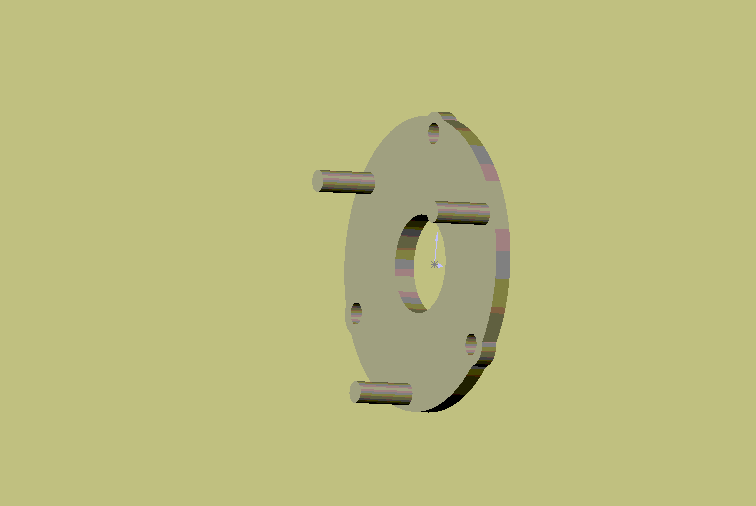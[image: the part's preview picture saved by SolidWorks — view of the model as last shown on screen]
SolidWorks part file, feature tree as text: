
SOLIDWORKS PART (.sldprt)
format: sldprt  version: not decoded by parser v0  size: 128,512 bytes
history: native  units: mm
features: sketch x5, plane x3, extrude x3, cut_extrude x2, material x1 (+8 scaffold rows collapsed)
feature tree (22):
  scaffold x8  (default folders/planes/origin — collapsed)
  material  "Matériau <non spécifié>"
  plane  "Plane1"
  plane  "Plane2"
  plane  "Plane3"
  sketch  "Esquisse1"  dims[D1=27.0mm D2=4.0mm D4=4.0mm D3=12.0mm]
  extrude  "Base-Extrusion"  Depth=1.5mm
  sketch  "Esquisse2"  dims[D1=2.0mm D2=2.0mm]
  cut_extrude  "Enlèv. mat.-Extru.1"  [1 undecoded]
  sketch  "Esquisse3"  dims[c1.D2=2.0mm c1.D1=18.0mm c2.D1=30.0deg c2.D3=12.0mm]
  extrude  "Boss.-Extru.1"  Depth=5.5mm
  sketch  "Esquisse4"  dims[D1=12.0mm]
  extrude  "Boss.-Extru.2"  Depth=0.5mm
  sketch  "Esquisse5"  dims[D1=9.0mm]
  cut_extrude  "Enlèv. mat.-Extru.2"  [1 undecoded]
decode coverage: 8 of 10 modeling features carry decoded parameters
note: 2 parameter values undecoded
note: suppression state not decoded; provenance and decode notes live in map.json
